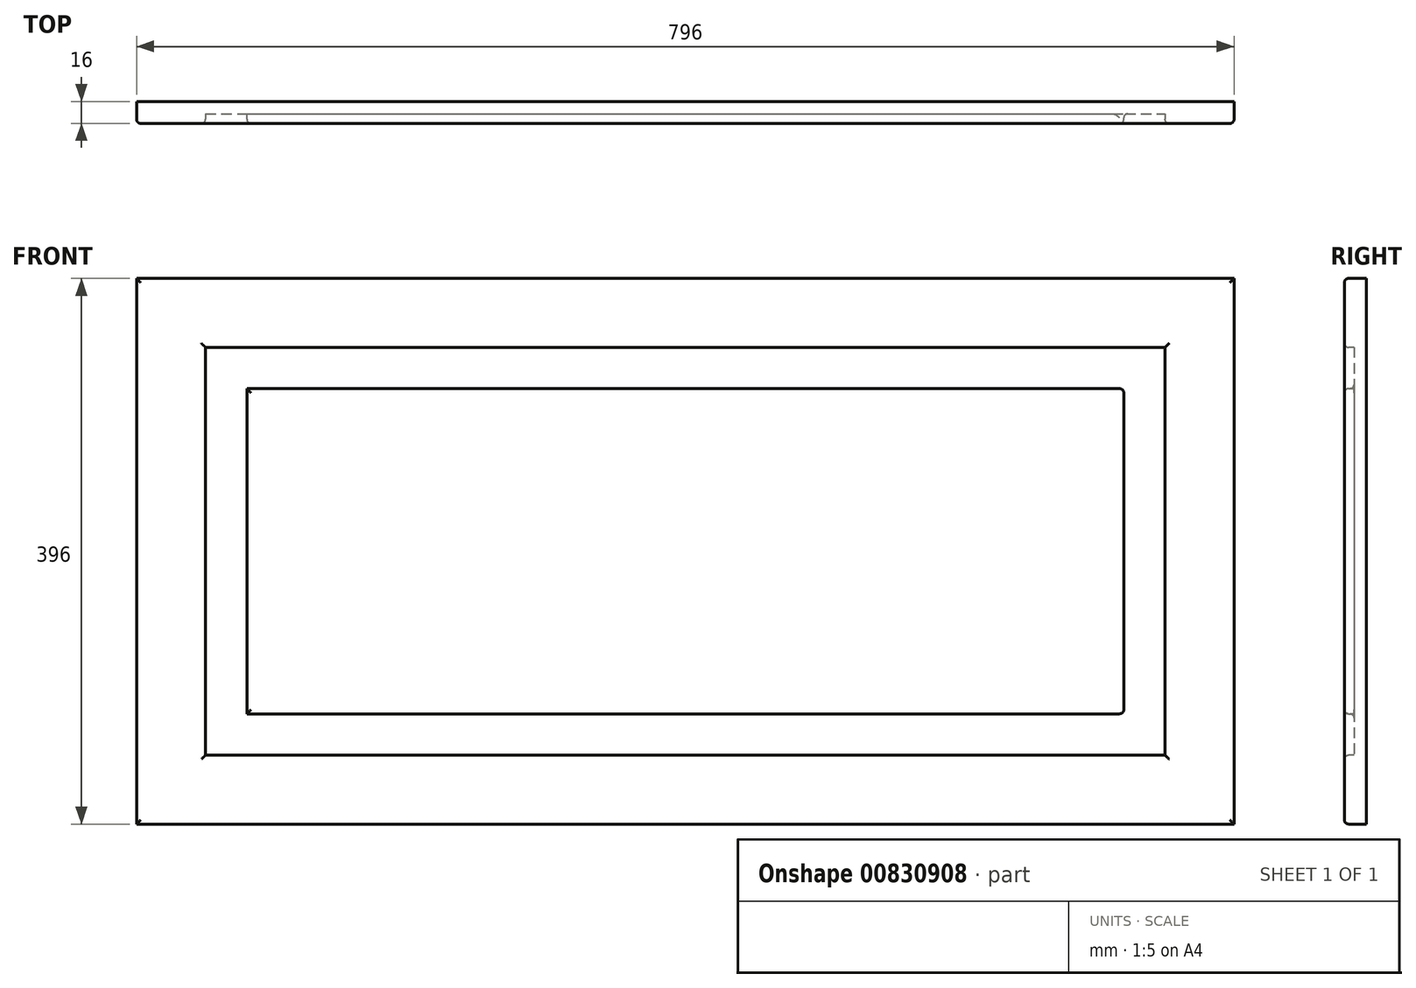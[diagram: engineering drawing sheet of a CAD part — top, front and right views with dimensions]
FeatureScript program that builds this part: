
annotation { "Feature Type Name" : "Feature", "Feature Type Description" : "" }
export const myFeature = defineFeature(function(context is Context, id is Id, definition is map)
    precondition{}
    {
        {
            var Q0;
            Q0=qCreatedBy(makeId("Front.planeOp"),FACE);
            var sketch = newSketch(context, id + "F0", { "sketchPlane" : qUnion([Q0])});
            skLineSegment(sketch, "E0.bottom", {"start": v(0, 0) * mm, "end": v(44.66, 0) * mm});
            skLineSegment(sketch, "E0.top", {"start": v(0, 33.8) * mm, "end": v(44.66, 33.8) * mm});
            skLineSegment(sketch, "E0.left", {"start": v(0, 0) * mm, "end": v(0, 33.8) * mm});
            skLineSegment(sketch, "E0.right", {"start": v(44.66, 0) * mm, "end": v(44.66, 33.8) * mm});
            skSolve(sketch);
        }
        {
            var Q0;
            Q0=makeQuery(id+"F0.imprint","IMPRINT",FACE,{"disambiguationData":[TD([[makeQuery(id+"F0.imprint","IMPRINT",EDGE,{"derivedFrom":sQuery(id+"F0.wireOp",EDGE,"E0.bottom")}),1.0]])]});
            extrude(context, id + "F1", {"entities" : qUnion([Q0]), "depth" : 16 * mm, "offsetDistance" : 25.4 * mm});
        }
        {
            var Q0;
            Q0=makeQuery(id+"F1.opExtrude","SWEPT_FACE",FACE,{"disambiguationData":[OSD([sQuery(id+"F0.wireOp",EDGE,"E0.bottom")])]});
            extrude(context, id + "F2", {"entities" : qUnion([Q0]), "operationType" : NewBodyOperationType.ADD, "oppositeDirection" : true, "depth" : 796 * mm, "offsetDistance" : 25 * mm});
        }
        {
            var Q0;
            {var subQ0=sQuery(id+"F0.wireOp",EDGE,"E0.left");Q0=makeQuery(id+"F2.boolean.opBoolean","MERGE",FACE,{"derivedFrom":[makeQuery(id+"F1.opExtrude","SWEPT_FACE",FACE,{"disambiguationData":[OSD([subQ0])]}),makeQuery(id+"F2.opExtrude","SWEPT_FACE",FACE,{"disambiguationData":[OSD([sQuery(id+"F0.wireOp",EDGE,"E0.bottom"),subQ0])]})]});}
            extrude(context, id + "F3", {"entities" : qUnion([Q0]), "operationType" : NewBodyOperationType.ADD, "oppositeDirection" : true, "depth" : 196 * mm, "offsetDistance" : 25 * mm});
        }
        {
            var Q0;
            {var subQ0=sQuery(id+"F0.wireOp",EDGE,"E0.left");var subQ1=sQuery(id+"F0.wireOp",EDGE,"E0.bottom");Q0=makeQuery(id+"F3.boolean.opBoolean","MERGE",FACE,{"derivedFrom":[makeQuery(id+"F2.boolean.opBoolean","MERGE",FACE,{"derivedFrom":[makeQuery(id+"F1.opExtrude","CAP_FACE",FACE,{"disambiguationData":[OSD([subQ1,sQuery(id+"F0.wireOp",EDGE,"E0.top"),subQ0,sQuery(id+"F0.wireOp",EDGE,"E0.right")])],"isStart":false}),makeQuery(id+"F2.opExtrude","SWEPT_FACE",FACE,{"disambiguationData":[OSD([subQ1]),TDD([makeQuery(id+"F1.opExtrude","CAP_EDGE",EDGE,{"disambiguationData":[OSD([subQ1])],"isStart":false})])]})]}),makeQuery(id+"F3.opExtrude","SWEPT_FACE",FACE,{"disambiguationData":[OSD([subQ1,subQ0]),TDD([makeQuery(id+"F2.boolean.opBoolean","MERGE",EDGE,{"derivedFrom":[makeQuery(id+"F1.opExtrude","CAP_EDGE",EDGE,{"disambiguationData":[OSD([subQ0])],"isStart":false}),makeQuery(id+"F2.opExtrude","SWEPT_EDGE",EDGE,{"disambiguationData":[OSD([subQ1,subQ0]),TDD([makeQuery(id+"F1.opExtrude","CAP_VERTEX",VERTEX,{"disambiguationData":[OSD([subQ1,subQ0])],"isStart":false})])]})]})])]})]});}
            var sketch = newSketch(context, id + "F4", { "sketchPlane" : qUnion([Q0])});
            skLineSegment(sketch, "E1.bottom", {"start": v(59.7, 646.67) * mm, "end": v(128.66, 646.67) * mm});
            skLineSegment(sketch, "E1.top", {"start": v(59.7, 152.97) * mm, "end": v(128.66, 152.97) * mm});
            skLineSegment(sketch, "E1.left", {"start": v(59.7, 646.67) * mm, "end": v(59.7, 152.97) * mm});
            skLineSegment(sketch, "E1.right", {"start": v(128.66, 646.67) * mm, "end": v(128.66, 152.97) * mm});
            skSolve(sketch);
        }
        {
            var Q0;
            Q0=makeQuery(id+"F4.imprint","IMPRINT",FACE,{"disambiguationData":[TD([[makeQuery(id+"F4.imprint","IMPRINT",EDGE,{"derivedFrom":sQuery(id+"F4.wireOp",EDGE,"E1.bottom")}),-1.0]])]});
            extrude(context, id + "F5", {"entities" : qUnion([Q0]), "operationType" : NewBodyOperationType.REMOVE, "oppositeDirection" : true, "depth" : 7 * mm, "offsetDistance" : 25 * mm});
        }
        {
            var Q0;
            Q0=makeQuery(id+"F5.boolean.opBoolean","COPY",FACE,{"derivedFrom":makeQuery(id+"F5.opExtrude","SWEPT_FACE",FACE,{"disambiguationData":[OSD([sQuery(id+"F4.wireOp",EDGE,"E1.left")])]})});
            extrude(context, id + "F6", {"entities" : qUnion([Q0]), "operationType" : NewBodyOperationType.REMOVE, "oppositeDirection" : true, "depth" : 9.7 * mm, "offsetDistance" : 25 * mm});
        }
        {
            var Q0;
            {var subQ0=sQuery(id+"F4.wireOp",EDGE,"E1.bottom");Q0=makeQuery(id+"F6.boolean.opBoolean","MERGE",FACE,{"derivedFrom":[makeQuery(id+"F5.boolean.opBoolean","COPY",FACE,{"derivedFrom":makeQuery(id+"F5.opExtrude","SWEPT_FACE",FACE,{"disambiguationData":[OSD([subQ0])]})}),makeQuery(id+"F6.opExtrude","SWEPT_FACE",FACE,{"disambiguationData":[OSD([subQ0,sQuery(id+"F4.wireOp",EDGE,"E1.left")])]})]});}
            extrude(context, id + "F7", {"entities" : qUnion([Q0]), "operationType" : NewBodyOperationType.ADD, "oppositeDirection" : true, "depth" : 99.33 * mm, "offsetDistance" : 25 * mm});
        }
        {
            var Q0;
            {var subQ0=sQuery(id+"F4.wireOp",EDGE,"E1.bottom");Q0=makeQuery(id+"F6.boolean.opBoolean","MERGE",FACE,{"derivedFrom":[makeQuery(id+"F5.boolean.opBoolean","COPY",FACE,{"derivedFrom":makeQuery(id+"F5.opExtrude","SWEPT_FACE",FACE,{"disambiguationData":[OSD([subQ0])]})}),makeQuery(id+"F6.opExtrude","SWEPT_FACE",FACE,{"disambiguationData":[OSD([subQ0,sQuery(id+"F4.wireOp",EDGE,"E1.left")])]})]});}
            extrude(context, id + "F8", {"entities" : qUnion([Q0]), "operationType" : NewBodyOperationType.REMOVE, "oppositeDirection" : true, "depth" : 99.33 * mm, "offsetDistance" : 25 * mm});
        }
        {
            var Q0;
            {var subQ0=sQuery(id+"F4.wireOp",EDGE,"E1.right");Q0=makeQuery(id+"F8.boolean.opBoolean","MERGE",FACE,{"derivedFrom":[makeQuery(id+"F5.boolean.opBoolean","COPY",FACE,{"derivedFrom":makeQuery(id+"F5.opExtrude","SWEPT_FACE",FACE,{"disambiguationData":[OSD([subQ0])]})}),makeQuery(id+"F8.opExtrude","SWEPT_FACE",FACE,{"disambiguationData":[OSD([sQuery(id+"F4.wireOp",EDGE,"E1.bottom"),subQ0])]})]});}
            extrude(context, id + "F9", {"entities" : qUnion([Q0]), "operationType" : NewBodyOperationType.REMOVE, "oppositeDirection" : true, "depth" : 17.34 * mm, "offsetDistance" : 25 * mm});
        }
        {
            var Q0;
            {var subQ0=sQuery(id+"F4.wireOp",EDGE,"E1.top");Q0=makeQuery(id+"F9.boolean.opBoolean","MERGE",FACE,{"derivedFrom":[makeQuery(id+"F6.boolean.opBoolean","MERGE",FACE,{"derivedFrom":[makeQuery(id+"F5.boolean.opBoolean","COPY",FACE,{"derivedFrom":makeQuery(id+"F5.opExtrude","SWEPT_FACE",FACE,{"disambiguationData":[OSD([subQ0])]})}),makeQuery(id+"F6.opExtrude","SWEPT_FACE",FACE,{"disambiguationData":[OSD([subQ0,sQuery(id+"F4.wireOp",EDGE,"E1.left")])]})]}),makeQuery(id+"F9.opExtrude","SWEPT_FACE",FACE,{"disambiguationData":[OSD([subQ0,sQuery(id+"F4.wireOp",EDGE,"E1.right")])]})]});}
            extrude(context, id + "F10", {"entities" : qUnion([Q0]), "operationType" : NewBodyOperationType.REMOVE, "oppositeDirection" : true, "depth" : 102.97 * mm, "offsetDistance" : 25 * mm});
        }
        {
            var Q0;
            {var subQ0=sQuery(id+"F4.wireOp",EDGE,"E1.right");var subQ1=sQuery(id+"F4.wireOp",EDGE,"E1.top");var subQ2=sQuery(id+"F4.wireOp",EDGE,"E1.left");var subQ3=sQuery(id+"F4.wireOp",EDGE,"E1.bottom");Q0=makeQuery(id+"F10.boolean.opBoolean","MERGE",FACE,{"derivedFrom":[makeQuery(id+"F9.boolean.opBoolean","MERGE",FACE,{"derivedFrom":[makeQuery(id+"F8.boolean.opBoolean","MERGE",FACE,{"derivedFrom":[makeQuery(id+"F6.boolean.opBoolean","MERGE",FACE,{"derivedFrom":[makeQuery(id+"F5.boolean.opBoolean","COPY",FACE,{"derivedFrom":makeQuery(id+"F5.opExtrude","CAP_FACE",FACE,{"disambiguationData":[OSD([subQ3,subQ1,subQ2,subQ0])],"isStart":false})}),makeQuery(id+"F6.opExtrude","SWEPT_FACE",FACE,{"disambiguationData":[OSD([subQ2]),TDD([makeQuery(id+"F5.boolean.opBoolean","COPY",EDGE,{"derivedFrom":makeQuery(id+"F5.opExtrude","CAP_EDGE",EDGE,{"disambiguationData":[OSD([subQ2])],"isStart":false})})])]})]}),makeQuery(id+"F8.opExtrude","SWEPT_FACE",FACE,{"disambiguationData":[OSD([subQ3,subQ2]),TDD([makeQuery(id+"F6.boolean.opBoolean","MERGE",EDGE,{"derivedFrom":[makeQuery(id+"F5.boolean.opBoolean","COPY",EDGE,{"derivedFrom":makeQuery(id+"F5.opExtrude","CAP_EDGE",EDGE,{"disambiguationData":[OSD([subQ3])],"isStart":false})}),makeQuery(id+"F6.opExtrude","SWEPT_EDGE",EDGE,{"disambiguationData":[OSD([subQ3,subQ2]),TDD([makeQuery(id+"F5.boolean.opBoolean","COPY",VERTEX,{"derivedFrom":makeQuery(id+"F5.opExtrude","CAP_VERTEX",VERTEX,{"disambiguationData":[OSD([subQ3,subQ2])],"isStart":false})})])]})]})])]})]}),makeQuery(id+"F9.opExtrude","SWEPT_FACE",FACE,{"disambiguationData":[OSD([subQ3,subQ0]),TDD([makeQuery(id+"F8.boolean.opBoolean","MERGE",EDGE,{"derivedFrom":[makeQuery(id+"F5.boolean.opBoolean","COPY",EDGE,{"derivedFrom":makeQuery(id+"F5.opExtrude","CAP_EDGE",EDGE,{"disambiguationData":[OSD([subQ0])],"isStart":false})}),makeQuery(id+"F8.opExtrude","SWEPT_EDGE",EDGE,{"disambiguationData":[OSD([subQ3,subQ0]),TDD([makeQuery(id+"F5.boolean.opBoolean","COPY",VERTEX,{"derivedFrom":makeQuery(id+"F5.opExtrude","CAP_VERTEX",VERTEX,{"disambiguationData":[OSD([subQ3,subQ0])],"isStart":false})})])]})]})])]})]}),makeQuery(id+"F10.opExtrude","SWEPT_FACE",FACE,{"disambiguationData":[OSD([subQ1,subQ2,subQ0]),TDD([makeQuery(id+"F9.boolean.opBoolean","MERGE",EDGE,{"derivedFrom":[makeQuery(id+"F6.boolean.opBoolean","MERGE",EDGE,{"derivedFrom":[makeQuery(id+"F5.boolean.opBoolean","COPY",EDGE,{"derivedFrom":makeQuery(id+"F5.opExtrude","CAP_EDGE",EDGE,{"disambiguationData":[OSD([subQ1])],"isStart":false})}),makeQuery(id+"F6.opExtrude","SWEPT_EDGE",EDGE,{"disambiguationData":[OSD([subQ1,subQ2]),TDD([makeQuery(id+"F5.boolean.opBoolean","COPY",VERTEX,{"derivedFrom":makeQuery(id+"F5.opExtrude","CAP_VERTEX",VERTEX,{"disambiguationData":[OSD([subQ1,subQ2])],"isStart":false})})])]})]}),makeQuery(id+"F9.opExtrude","SWEPT_EDGE",EDGE,{"disambiguationData":[OSD([subQ1,subQ0]),TDD([makeQuery(id+"F5.boolean.opBoolean","COPY",VERTEX,{"derivedFrom":makeQuery(id+"F5.opExtrude","CAP_VERTEX",VERTEX,{"disambiguationData":[OSD([subQ1,subQ0])],"isStart":false})})])]})]})])]})]});}
            var sketch = newSketch(context, id + "F11", { "sketchPlane" : qUnion([Q0])});
            skLineSegment(sketch, "E2.bottom", {"start": v(74.13, 678.73) * mm, "end": v(109.41, 678.73) * mm});
            skLineSegment(sketch, "E2.top", {"start": v(74.13, 186.63) * mm, "end": v(109.41, 186.63) * mm});
            skLineSegment(sketch, "E2.left", {"start": v(74.13, 678.73) * mm, "end": v(74.13, 186.63) * mm});
            skLineSegment(sketch, "E2.right", {"start": v(109.41, 678.73) * mm, "end": v(109.41, 186.63) * mm});
            skSolve(sketch);
        }
        {
            var Q0;
            Q0=makeQuery(id+"F11.imprint","IMPRINT",FACE,{"disambiguationData":[TD([[makeQuery(id+"F11.imprint","IMPRINT",EDGE,{"derivedFrom":sQuery(id+"F11.wireOp",EDGE,"E2.bottom")}),-1.0]])]});
            extrude(context, id + "F12", {"entities" : qUnion([Q0]), "operationType" : NewBodyOperationType.ADD, "depth" : 7 * mm, "offsetDistance" : 25 * mm});
        }
        {
            var Q0;
            Q0=makeQuery(id+"F12.opExtrude","SWEPT_FACE",FACE,{"disambiguationData":[OSD([sQuery(id+"F11.wireOp",EDGE,"E2.bottom")])]});
            extrude(context, id + "F13", {"entities" : qUnion([Q0]), "operationType" : NewBodyOperationType.ADD, "depth" : 37.27 * mm, "offsetDistance" : 25 * mm});
        }
        {
            var Q0;
            {var subQ0=sQuery(id+"F11.wireOp",EDGE,"E2.right");Q0=makeQuery(id+"F13.boolean.opBoolean","MERGE",FACE,{"derivedFrom":[makeQuery(id+"F12.opExtrude","SWEPT_FACE",FACE,{"disambiguationData":[OSD([subQ0])]}),makeQuery(id+"F13.opExtrude","SWEPT_FACE",FACE,{"disambiguationData":[OSD([sQuery(id+"F11.wireOp",EDGE,"E2.bottom"),subQ0])]})]});}
            extrude(context, id + "F14", {"entities" : qUnion([Q0]), "operationType" : NewBodyOperationType.ADD, "depth" : 6.58 * mm, "offsetDistance" : 25 * mm});
        }
        {
            var Q0;
            {var subQ0=sQuery(id+"F11.wireOp",EDGE,"E2.top");Q0=makeQuery(id+"F14.boolean.opBoolean","MERGE",FACE,{"derivedFrom":[makeQuery(id+"F12.opExtrude","SWEPT_FACE",FACE,{"disambiguationData":[OSD([subQ0])]}),makeQuery(id+"F14.opExtrude","SWEPT_FACE",FACE,{"disambiguationData":[OSD([subQ0,sQuery(id+"F11.wireOp",EDGE,"E2.right")])]})]});}
            extrude(context, id + "F15", {"entities" : qUnion([Q0]), "operationType" : NewBodyOperationType.ADD, "depth" : 106.63 * mm, "offsetDistance" : 25 * mm});
        }
        {
            var Q0;
            {var subQ0=sQuery(id+"F11.wireOp",EDGE,"E2.left");Q0=makeQuery(id+"F15.boolean.opBoolean","MERGE",FACE,{"derivedFrom":[makeQuery(id+"F13.boolean.opBoolean","MERGE",FACE,{"derivedFrom":[makeQuery(id+"F12.opExtrude","SWEPT_FACE",FACE,{"disambiguationData":[OSD([subQ0])]}),makeQuery(id+"F13.opExtrude","SWEPT_FACE",FACE,{"disambiguationData":[OSD([sQuery(id+"F11.wireOp",EDGE,"E2.bottom"),subQ0])]})]}),makeQuery(id+"F15.opExtrude","SWEPT_FACE",FACE,{"disambiguationData":[OSD([sQuery(id+"F11.wireOp",EDGE,"E2.top"),subQ0])]})]});}
            extrude(context, id + "F16", {"entities" : qUnion([Q0]), "operationType" : NewBodyOperationType.REMOVE, "oppositeDirection" : true, "depth" : 5.87 * mm, "offsetDistance" : 25 * mm});
        }
        {
            var Q0;
            Q0=makeQuery(id+"F3.opExtrude","CAP_FACE",FACE,{"disambiguationData":[OSD([sQuery(id+"F0.wireOp",EDGE,"E0.bottom"),sQuery(id+"F0.wireOp",EDGE,"E0.left")])],"isStart":false});
            extrude(context, id + "F17", {"entities" : qUnion([Q0]), "operationType" : NewBodyOperationType.ADD, "depth" : 200 * mm, "offsetDistance" : 25 * mm});
        }
        {
            var Q0;
            {var subQ0=sQuery(id+"F4.wireOp",EDGE,"E1.right");Q0=makeQuery(id+"F10.boolean.opBoolean","MERGE",FACE,{"derivedFrom":[makeQuery(id+"F9.boolean.opBoolean","COPY",FACE,{"derivedFrom":makeQuery(id+"F9.opExtrude","CAP_FACE",FACE,{"disambiguationData":[OSD([sQuery(id+"F4.wireOp",EDGE,"E1.bottom"),subQ0])],"isStart":false})}),makeQuery(id+"F10.opExtrude","SWEPT_FACE",FACE,{"disambiguationData":[OSD([sQuery(id+"F4.wireOp",EDGE,"E1.top"),subQ0])]})]});}
            extrude(context, id + "F18", {"entities" : qUnion([Q0]), "operationType" : NewBodyOperationType.REMOVE, "oppositeDirection" : true, "depth" : 200 * mm, "offsetDistance" : 25 * mm});
        }
        {
            var Q0;
            {var subQ0=sQuery(id+"F11.wireOp",EDGE,"E2.right");var subQ1=sQuery(id+"F11.wireOp",EDGE,"E2.top");Q0=makeQuery(id+"F15.boolean.opBoolean","MERGE",FACE,{"derivedFrom":[makeQuery(id+"F14.opExtrude","CAP_FACE",FACE,{"disambiguationData":[OSD([sQuery(id+"F11.wireOp",EDGE,"E2.bottom"),subQ0])],"isStart":false}),makeQuery(id+"F15.opExtrude","SWEPT_FACE",FACE,{"disambiguationData":[OSD([subQ1,subQ0]),TDD([makeQuery(id+"F14.opExtrude","CAP_EDGE",EDGE,{"disambiguationData":[OSD([subQ1,subQ0])],"isStart":false})])]})]});}
            extrude(context, id + "F19", {"entities" : qUnion([Q0]), "operationType" : NewBodyOperationType.ADD, "depth" : 200 * mm, "offsetDistance" : 25 * mm});
        }
        {
            var Q0;
            Q0=makeQuery(id+"F17.opExtrude","CAP_FACE",FACE,{"disambiguationData":[OSD([sQuery(id+"F0.wireOp",EDGE,"E0.bottom"),sQuery(id+"F0.wireOp",EDGE,"E0.left")])],"isStart":false});
            extrude(context, id + "F20", {"entities" : qUnion([Q0]), "operationType" : NewBodyOperationType.ADD, "depth" : 200 * mm, "offsetDistance" : 25 * mm});
        }
        {
            var Q0;
            Q0=makeQuery(id+"F18.boolean.opBoolean","COPY",FACE,{"derivedFrom":makeQuery(id+"F18.opExtrude","CAP_FACE",FACE,{"disambiguationData":[OSD([sQuery(id+"F4.wireOp",EDGE,"E1.bottom"),sQuery(id+"F4.wireOp",EDGE,"E1.top"),sQuery(id+"F4.wireOp",EDGE,"E1.right")])],"isStart":false})});
            extrude(context, id + "F21", {"entities" : qUnion([Q0]), "operationType" : NewBodyOperationType.REMOVE, "oppositeDirection" : true, "depth" : 200 * mm, "offsetDistance" : 25 * mm});
        }
        {
            var Q0;
            Q0=makeQuery(id+"F19.opExtrude","CAP_FACE",FACE,{"disambiguationData":[OSD([sQuery(id+"F11.wireOp",EDGE,"E2.bottom"),sQuery(id+"F11.wireOp",EDGE,"E2.top"),sQuery(id+"F11.wireOp",EDGE,"E2.right")])],"isStart":false});
            extrude(context, id + "F22", {"entities" : qUnion([Q0]), "operationType" : NewBodyOperationType.ADD, "depth" : 200 * mm, "offsetDistance" : 25 * mm});
        }
        {
            var Q0;
            {var subQ0=sQuery(id+"F11.wireOp",EDGE,"E2.right");var subQ1=sQuery(id+"F11.wireOp",EDGE,"E2.top");Q0=makeQuery(id+"F22.boolean.opBoolean","MERGE",FACE,{"derivedFrom":[makeQuery(id+"F19.boolean.opBoolean","MERGE",FACE,{"derivedFrom":[makeQuery(id+"F15.opExtrude","CAP_FACE",FACE,{"disambiguationData":[OSD([subQ1,subQ0])],"isStart":false}),makeQuery(id+"F19.opExtrude","SWEPT_FACE",FACE,{"disambiguationData":[OSD([subQ1,subQ0])]})]}),makeQuery(id+"F22.opExtrude","SWEPT_FACE",FACE,{"disambiguationData":[OSD([subQ1,subQ0])]})]});}
            extrude(context, id + "F23", {"entities" : qUnion([Q0]), "operationType" : NewBodyOperationType.REMOVE, "oppositeDirection" : true, "depth" : 600 * mm, "offsetDistance" : 25 * mm});
        }
        {
            var Q0;
            {var subQ0=sQuery(id+"F4.wireOp",EDGE,"E1.right");var subQ1=sQuery(id+"F4.wireOp",EDGE,"E1.top");Q0=makeQuery(id+"F21.boolean.opBoolean","MERGE",FACE,{"derivedFrom":[makeQuery(id+"F18.boolean.opBoolean","MERGE",FACE,{"derivedFrom":[makeQuery(id+"F10.boolean.opBoolean","COPY",FACE,{"derivedFrom":makeQuery(id+"F10.opExtrude","CAP_FACE",FACE,{"disambiguationData":[OSD([subQ1,sQuery(id+"F4.wireOp",EDGE,"E1.left"),subQ0])],"isStart":false})}),makeQuery(id+"F18.opExtrude","SWEPT_FACE",FACE,{"disambiguationData":[OSD([subQ1,subQ0])]})]}),makeQuery(id+"F21.opExtrude","SWEPT_FACE",FACE,{"disambiguationData":[OSD([subQ1,subQ0])]})]});}
            extrude(context, id + "F24", {"entities" : qUnion([Q0]), "operationType" : NewBodyOperationType.ADD, "depth" : 600 * mm, "offsetDistance" : 25 * mm});
        }
        {
            var Q0;
            {var subQ0=sQuery(id+"F0.wireOp",EDGE,"E0.left");var subQ1=sQuery(id+"F0.wireOp",EDGE,"E0.bottom");var subQ2=makeQuery(id+"F1.opExtrude","SWEPT_EDGE",EDGE,{"disambiguationData":[OSD([subQ1,subQ0])]});var subQ3=makeQuery(id+"F3.opExtrude","CAP_EDGE",EDGE,{"disambiguationData":[OSD([subQ1,subQ0]),TDD([subQ2])],"isStart":false});Q0=makeQuery(id+"F20.boolean.opBoolean","MERGE",FACE,{"derivedFrom":[makeQuery(id+"F17.boolean.opBoolean","MERGE",FACE,{"derivedFrom":[makeQuery(id+"F3.boolean.opBoolean","MERGE",FACE,{"derivedFrom":[makeQuery(id+"F1.opExtrude","SWEPT_FACE",FACE,{"disambiguationData":[OSD([subQ1])]}),makeQuery(id+"F3.opExtrude","SWEPT_FACE",FACE,{"disambiguationData":[OSD([subQ1,subQ0]),TDD([subQ2])]})]}),makeQuery(id+"F17.opExtrude","SWEPT_FACE",FACE,{"disambiguationData":[OSD([subQ1,subQ0]),TDD([subQ3])]})]}),makeQuery(id+"F20.opExtrude","SWEPT_FACE",FACE,{"disambiguationData":[OSD([subQ1,subQ0]),TDD([makeQuery(id+"F17.opExtrude","CAP_EDGE",EDGE,{"disambiguationData":[OSD([subQ1,subQ0]),TDD([subQ3])],"isStart":false})])]})]});}
            extrude(context, id + "F25", {"entities" : qUnion([Q0]), "operationType" : NewBodyOperationType.REMOVE, "oppositeDirection" : true, "depth" : 600 * mm, "offsetDistance" : 25 * mm});
        }
        {
            var Q0;
            Q0=makeQuery(id+"F25.boolean.opBoolean","COPY",FACE,{"derivedFrom":makeQuery(id+"F25.opExtrude","CAP_FACE",FACE,{"disambiguationData":[OSD([sQuery(id+"F0.wireOp",EDGE,"E0.bottom"),sQuery(id+"F0.wireOp",EDGE,"E0.left")])],"isStart":false})});
            extrude(context, id + "F26", {"entities" : qUnion([Q0]), "operationType" : NewBodyOperationType.ADD, "depth" : 200 * mm, "offsetDistance" : 25 * mm});
        }
        {
            var Q0;
            Q0=makeQuery(id+"F24.opExtrude","CAP_FACE",FACE,{"disambiguationData":[OSD([sQuery(id+"F4.wireOp",EDGE,"E1.top"),sQuery(id+"F4.wireOp",EDGE,"E1.left"),sQuery(id+"F4.wireOp",EDGE,"E1.right")])],"isStart":false});
            extrude(context, id + "F27", {"entities" : qUnion([Q0]), "operationType" : NewBodyOperationType.REMOVE, "oppositeDirection" : true, "depth" : 200 * mm, "offsetDistance" : 25 * mm});
        }
        {
            var Q0;
            Q0=makeQuery(id+"F23.boolean.opBoolean","COPY",FACE,{"derivedFrom":makeQuery(id+"F23.opExtrude","CAP_FACE",FACE,{"disambiguationData":[OSD([sQuery(id+"F11.wireOp",EDGE,"E2.top"),sQuery(id+"F11.wireOp",EDGE,"E2.right")])],"isStart":false})});
            extrude(context, id + "F28", {"entities" : qUnion([Q0]), "operationType" : NewBodyOperationType.ADD, "depth" : 200 * mm, "offsetDistance" : 25 * mm});
        }
        {
            var Q0;
            {var subQ0=sQuery(id+"F0.wireOp",EDGE,"E0.left");var subQ1=sQuery(id+"F0.wireOp",EDGE,"E0.bottom");Q0=makeQuery(id+"F26.boolean.opBoolean","MERGE",FACE,{"derivedFrom":[makeQuery(id+"F20.opExtrude","CAP_FACE",FACE,{"disambiguationData":[OSD([subQ1,subQ0])],"isStart":false}),makeQuery(id+"F26.opExtrude","SWEPT_FACE",FACE,{"disambiguationData":[OSD([subQ1,subQ0]),TDD([makeQuery(id+"F25.boolean.opBoolean","COPY",EDGE,{"derivedFrom":makeQuery(id+"F25.opExtrude","CAP_EDGE",EDGE,{"disambiguationData":[OSD([subQ1,subQ0]),TDD([makeQuery(id+"F20.opExtrude","CAP_EDGE",EDGE,{"disambiguationData":[OSD([subQ1,subQ0]),TDD([makeQuery(id+"F17.opExtrude","CAP_EDGE",EDGE,{"disambiguationData":[OSD([subQ1,subQ0]),TDD([makeQuery(id+"F3.opExtrude","CAP_EDGE",EDGE,{"disambiguationData":[OSD([subQ1,subQ0]),TDD([makeQuery(id+"F1.opExtrude","SWEPT_EDGE",EDGE,{"disambiguationData":[OSD([subQ1,subQ0])]})])],"isStart":false})])],"isStart":false})])],"isStart":false})])],"isStart":false})})])]})]});}
            extrude(context, id + "F29", {"entities" : qUnion([Q0]), "operationType" : NewBodyOperationType.ADD, "depth" : 200 * mm, "offsetDistance" : 25 * mm});
        }
        {
            var Q0;
            {var subQ0=sQuery(id+"F4.wireOp",EDGE,"E1.right");var subQ1=sQuery(id+"F4.wireOp",EDGE,"E1.top");Q0=makeQuery(id+"F27.boolean.opBoolean","MERGE",FACE,{"derivedFrom":[makeQuery(id+"F21.boolean.opBoolean","COPY",FACE,{"derivedFrom":makeQuery(id+"F21.opExtrude","CAP_FACE",FACE,{"disambiguationData":[OSD([sQuery(id+"F4.wireOp",EDGE,"E1.bottom"),subQ1,subQ0])],"isStart":false})}),makeQuery(id+"F27.opExtrude","SWEPT_FACE",FACE,{"disambiguationData":[OSD([subQ1,subQ0])]})]});}
            extrude(context, id + "F30", {"entities" : qUnion([Q0]), "operationType" : NewBodyOperationType.REMOVE, "oppositeDirection" : true, "depth" : 200 * mm, "offsetDistance" : 25 * mm});
        }
        {
            var Q0;
            {var subQ0=sQuery(id+"F11.wireOp",EDGE,"E2.right");var subQ1=sQuery(id+"F11.wireOp",EDGE,"E2.top");Q0=makeQuery(id+"F28.boolean.opBoolean","MERGE",FACE,{"derivedFrom":[makeQuery(id+"F22.opExtrude","CAP_FACE",FACE,{"disambiguationData":[OSD([sQuery(id+"F11.wireOp",EDGE,"E2.bottom"),subQ1,subQ0])],"isStart":false}),makeQuery(id+"F28.opExtrude","SWEPT_FACE",FACE,{"disambiguationData":[OSD([subQ1,subQ0]),TDD([makeQuery(id+"F23.boolean.opBoolean","COPY",EDGE,{"derivedFrom":makeQuery(id+"F23.opExtrude","CAP_EDGE",EDGE,{"disambiguationData":[OSD([subQ1,subQ0]),TDD([makeQuery(id+"F22.opExtrude","CAP_EDGE",EDGE,{"disambiguationData":[OSD([subQ1,subQ0])],"isStart":false})])],"isStart":false})})])]})]});}
            extrude(context, id + "F31", {"entities" : qUnion([Q0]), "operationType" : NewBodyOperationType.ADD, "depth" : 200 * mm, "offsetDistance" : 25 * mm});
        }
        {
            var Q0;
            {var subQ0=sQuery(id+"F11.wireOp",EDGE,"E2.right");var subQ1=sQuery(id+"F11.wireOp",EDGE,"E2.top");Q0=makeQuery(id+"F31.boolean.opBoolean","MERGE",FACE,{"derivedFrom":[makeQuery(id+"F28.opExtrude","CAP_FACE",FACE,{"disambiguationData":[OSD([subQ1,subQ0])],"isStart":false}),makeQuery(id+"F31.opExtrude","SWEPT_FACE",FACE,{"disambiguationData":[OSD([subQ1,subQ0])]})]});}
            extrude(context, id + "F32", {"entities" : qUnion([Q0]), "operationType" : NewBodyOperationType.REMOVE, "oppositeDirection" : true, "depth" : 200 * mm, "offsetDistance" : 25 * mm});
        }
        {
            var Q0;
            {var subQ0=sQuery(id+"F4.wireOp",EDGE,"E1.right");var subQ1=sQuery(id+"F4.wireOp",EDGE,"E1.top");Q0=makeQuery(id+"F30.boolean.opBoolean","MERGE",FACE,{"derivedFrom":[makeQuery(id+"F27.boolean.opBoolean","COPY",FACE,{"derivedFrom":makeQuery(id+"F27.opExtrude","CAP_FACE",FACE,{"disambiguationData":[OSD([subQ1,sQuery(id+"F4.wireOp",EDGE,"E1.left"),subQ0])],"isStart":false})}),makeQuery(id+"F30.opExtrude","SWEPT_FACE",FACE,{"disambiguationData":[OSD([subQ1,subQ0])]})]});}
            extrude(context, id + "F33", {"entities" : qUnion([Q0]), "operationType" : NewBodyOperationType.ADD, "depth" : 200 * mm, "offsetDistance" : 25 * mm});
        }
        {
            var Q0;
            {var subQ0=sQuery(id+"F0.wireOp",EDGE,"E0.left");var subQ1=sQuery(id+"F0.wireOp",EDGE,"E0.bottom");Q0=makeQuery(id+"F29.boolean.opBoolean","MERGE",FACE,{"derivedFrom":[makeQuery(id+"F26.opExtrude","CAP_FACE",FACE,{"disambiguationData":[OSD([subQ1,subQ0])],"isStart":false}),makeQuery(id+"F29.opExtrude","SWEPT_FACE",FACE,{"disambiguationData":[OSD([subQ1,subQ0]),TDD([makeQuery(id+"F26.opExtrude","CAP_EDGE",EDGE,{"disambiguationData":[OSD([subQ1,subQ0]),TDD([makeQuery(id+"F25.boolean.opBoolean","COPY",EDGE,{"derivedFrom":makeQuery(id+"F25.opExtrude","CAP_EDGE",EDGE,{"disambiguationData":[OSD([subQ1,subQ0]),TDD([makeQuery(id+"F20.opExtrude","CAP_EDGE",EDGE,{"disambiguationData":[OSD([subQ1,subQ0]),TDD([makeQuery(id+"F17.opExtrude","CAP_EDGE",EDGE,{"disambiguationData":[OSD([subQ1,subQ0]),TDD([makeQuery(id+"F3.opExtrude","CAP_EDGE",EDGE,{"disambiguationData":[OSD([subQ1,subQ0]),TDD([makeQuery(id+"F1.opExtrude","SWEPT_EDGE",EDGE,{"disambiguationData":[OSD([subQ1,subQ0])]})])],"isStart":false})])],"isStart":false})])],"isStart":false})])],"isStart":false})})])],"isStart":false})])]})]});}
            extrude(context, id + "F34", {"entities" : qUnion([Q0]), "operationType" : NewBodyOperationType.REMOVE, "oppositeDirection" : true, "depth" : 200 * mm, "offsetDistance" : 25 * mm});
        }
        {
            var Q0;
            Q0=makeQuery(id+"F34.boolean.opBoolean","COPY",FACE,{"derivedFrom":makeQuery(id+"F34.opExtrude","CAP_FACE",FACE,{"disambiguationData":[OSD([sQuery(id+"F0.wireOp",EDGE,"E0.bottom"),sQuery(id+"F0.wireOp",EDGE,"E0.left")])],"isStart":false})});
            extrude(context, id + "F35", {"entities" : qUnion([Q0]), "operationType" : NewBodyOperationType.ADD, "depth" : 200 * mm, "offsetDistance" : 25 * mm});
        }
        {
            var Q0;
            Q0=makeQuery(id+"F33.opExtrude","CAP_FACE",FACE,{"disambiguationData":[OSD([sQuery(id+"F4.wireOp",EDGE,"E1.top"),sQuery(id+"F4.wireOp",EDGE,"E1.left"),sQuery(id+"F4.wireOp",EDGE,"E1.right")])],"isStart":false});
            extrude(context, id + "F36", {"entities" : qUnion([Q0]), "operationType" : NewBodyOperationType.REMOVE, "oppositeDirection" : true, "depth" : 200 * mm, "offsetDistance" : 25 * mm});
        }
        {
            var Q0;
            Q0=makeQuery(id+"F32.boolean.opBoolean","COPY",FACE,{"derivedFrom":makeQuery(id+"F32.opExtrude","CAP_FACE",FACE,{"disambiguationData":[OSD([sQuery(id+"F11.wireOp",EDGE,"E2.top"),sQuery(id+"F11.wireOp",EDGE,"E2.right")])],"isStart":false})});
            extrude(context, id + "F37", {"entities" : qUnion([Q0]), "operationType" : NewBodyOperationType.ADD, "depth" : 200 * mm, "offsetDistance" : 25 * mm});
        }
        {
            var Q0;
            {var subQ0=sQuery(id+"F11.wireOp",EDGE,"E2.right");var subQ1=sQuery(id+"F11.wireOp",EDGE,"E2.top");var subQ2=makeQuery(id+"F12.opExtrude","CAP_VERTEX",VERTEX,{"disambiguationData":[OSD([subQ1,subQ0])],"isStart":false});var subQ3=makeQuery(id+"F14.opExtrude","CAP_VERTEX",VERTEX,{"disambiguationData":[OSD([subQ1,subQ0]),TDD([subQ2])],"isStart":false});var subQ4=makeQuery(id+"F15.opExtrude","CAP_VERTEX",VERTEX,{"disambiguationData":[OSD([subQ1,subQ0]),TDD([subQ3])],"isStart":false});var subQ5=makeQuery(id+"F19.opExtrude","CAP_VERTEX",VERTEX,{"disambiguationData":[OSD([subQ1,subQ0]),TDD([subQ4])],"isStart":false});var subQ6=makeQuery(id+"F23.boolean.opBoolean","COPY",VERTEX,{"derivedFrom":makeQuery(id+"F23.opExtrude","CAP_VERTEX",VERTEX,{"disambiguationData":[OSD([subQ1,subQ0]),TDD([makeQuery(id+"F22.opExtrude","CAP_VERTEX",VERTEX,{"disambiguationData":[OSD([subQ1,subQ0]),TDD([subQ5])],"isStart":false})])],"isStart":false})});var subQ7=makeQuery(id+"F14.boolean.opBoolean","MERGE",EDGE,{"derivedFrom":[makeQuery(id+"F12.opExtrude","CAP_EDGE",EDGE,{"disambiguationData":[OSD([subQ1])],"isStart":false}),makeQuery(id+"F14.opExtrude","SWEPT_EDGE",EDGE,{"disambiguationData":[OSD([subQ1,subQ0]),TDD([subQ2])]})]});var subQ8=makeQuery(id+"F23.boolean.opBoolean","COPY",EDGE,{"derivedFrom":makeQuery(id+"F23.opExtrude","CAP_EDGE",EDGE,{"disambiguationData":[OSD([subQ1,subQ0]),TDD([makeQuery(id+"F22.boolean.opBoolean","MERGE",EDGE,{"derivedFrom":[makeQuery(id+"F19.boolean.opBoolean","MERGE",EDGE,{"derivedFrom":[makeQuery(id+"F15.opExtrude","CAP_EDGE",EDGE,{"disambiguationData":[OSD([subQ1,subQ0]),TDD([subQ7])],"isStart":false}),makeQuery(id+"F19.opExtrude","SWEPT_EDGE",EDGE,{"disambiguationData":[OSD([subQ1,subQ0]),TDD([subQ4])]})]}),makeQuery(id+"F22.opExtrude","SWEPT_EDGE",EDGE,{"disambiguationData":[OSD([subQ1,subQ0]),TDD([subQ5])]})]})])],"isStart":false})});var subQ9=sQuery(id+"F11.wireOp",EDGE,"E2.bottom");var subQ10=makeQuery(id+"F13.boolean.opBoolean","MERGE",EDGE,{"derivedFrom":[makeQuery(id+"F12.opExtrude","CAP_EDGE",EDGE,{"disambiguationData":[OSD([subQ0])],"isStart":false}),makeQuery(id+"F13.opExtrude","SWEPT_EDGE",EDGE,{"disambiguationData":[OSD([subQ9,subQ0]),TDD([makeQuery(id+"F12.opExtrude","CAP_VERTEX",VERTEX,{"disambiguationData":[OSD([subQ9,subQ0])],"isStart":false})])]})]});var subQ11=makeQuery(id+"F15.boolean.opBoolean","MERGE",EDGE,{"derivedFrom":[makeQuery(id+"F14.opExtrude","CAP_EDGE",EDGE,{"disambiguationData":[OSD([subQ9,subQ0]),TDD([subQ10])],"isStart":false}),makeQuery(id+"F15.opExtrude","SWEPT_EDGE",EDGE,{"disambiguationData":[OSD([subQ1,subQ0]),TDD([subQ3])]})]});var subQ12=makeQuery(id+"F19.opExtrude","CAP_EDGE",EDGE,{"disambiguationData":[OSD([subQ9,subQ1,subQ0]),TDD([subQ11])],"isStart":false});Q0=makeQuery(id+"F37.boolean.opBoolean","MERGE",FACE,{"derivedFrom":[makeQuery(id+"F31.boolean.opBoolean","MERGE",FACE,{"derivedFrom":[makeQuery(id+"F28.boolean.opBoolean","MERGE",FACE,{"derivedFrom":[makeQuery(id+"F22.boolean.opBoolean","MERGE",FACE,{"derivedFrom":[makeQuery(id+"F19.boolean.opBoolean","MERGE",FACE,{"derivedFrom":[makeQuery(id+"F15.boolean.opBoolean","MERGE",FACE,{"derivedFrom":[makeQuery(id+"F14.boolean.opBoolean","MERGE",FACE,{"derivedFrom":[makeQuery(id+"F13.boolean.opBoolean","MERGE",FACE,{"derivedFrom":[makeQuery(id+"F12.opExtrude","CAP_FACE",FACE,{"disambiguationData":[OSD([subQ9,subQ1,sQuery(id+"F11.wireOp",EDGE,"E2.left"),subQ0])],"isStart":false}),makeQuery(id+"F13.opExtrude","SWEPT_FACE",FACE,{"disambiguationData":[OSD([subQ9]),TDD([makeQuery(id+"F12.opExtrude","CAP_EDGE",EDGE,{"disambiguationData":[OSD([subQ9])],"isStart":false})])]})]}),makeQuery(id+"F14.opExtrude","SWEPT_FACE",FACE,{"disambiguationData":[OSD([subQ9,subQ0]),TDD([subQ10])]})]}),makeQuery(id+"F15.opExtrude","SWEPT_FACE",FACE,{"disambiguationData":[OSD([subQ1,subQ0]),TDD([subQ7])]})]}),makeQuery(id+"F19.opExtrude","SWEPT_FACE",FACE,{"disambiguationData":[OSD([subQ9,subQ1,subQ0]),TDD([subQ11])]})]}),makeQuery(id+"F22.opExtrude","SWEPT_FACE",FACE,{"disambiguationData":[OSD([subQ9,subQ1,subQ0]),TDD([subQ12])]})]}),makeQuery(id+"F28.opExtrude","SWEPT_FACE",FACE,{"disambiguationData":[OSD([subQ1,subQ0]),TDD([subQ8])]})]}),makeQuery(id+"F31.opExtrude","SWEPT_FACE",FACE,{"disambiguationData":[OSD([subQ9,subQ1,subQ0]),TDD([makeQuery(id+"F28.boolean.opBoolean","MERGE",EDGE,{"derivedFrom":[makeQuery(id+"F22.opExtrude","CAP_EDGE",EDGE,{"disambiguationData":[OSD([subQ9,subQ1,subQ0]),TDD([subQ12])],"isStart":false}),makeQuery(id+"F28.opExtrude","SWEPT_EDGE",EDGE,{"disambiguationData":[OSD([subQ1,subQ0]),TDD([subQ6])]})]})])]})]}),makeQuery(id+"F37.opExtrude","SWEPT_FACE",FACE,{"disambiguationData":[OSD([subQ1,subQ0]),TDD([makeQuery(id+"F32.boolean.opBoolean","COPY",EDGE,{"derivedFrom":makeQuery(id+"F32.opExtrude","CAP_EDGE",EDGE,{"disambiguationData":[OSD([subQ1,subQ0]),TDD([makeQuery(id+"F31.boolean.opBoolean","MERGE",EDGE,{"derivedFrom":[makeQuery(id+"F28.opExtrude","CAP_EDGE",EDGE,{"disambiguationData":[OSD([subQ1,subQ0]),TDD([subQ8])],"isStart":false}),makeQuery(id+"F31.opExtrude","SWEPT_EDGE",EDGE,{"disambiguationData":[OSD([subQ1,subQ0]),TDD([makeQuery(id+"F28.opExtrude","CAP_VERTEX",VERTEX,{"disambiguationData":[OSD([subQ1,subQ0]),TDD([subQ6])],"isStart":false})])]})]})])],"isStart":false})})])]})]});}
            var Q1;
            {var subQ0=sQuery(id+"F0.wireOp",EDGE,"E0.left");var subQ1=sQuery(id+"F0.wireOp",EDGE,"E0.bottom");var subQ2=makeQuery(id+"F1.opExtrude","CAP_VERTEX",VERTEX,{"disambiguationData":[OSD([subQ1,subQ0])],"isStart":false});var subQ3=makeQuery(id+"F3.opExtrude","CAP_VERTEX",VERTEX,{"disambiguationData":[OSD([subQ1,subQ0]),TDD([subQ2])],"isStart":false});var subQ4=makeQuery(id+"F17.opExtrude","CAP_VERTEX",VERTEX,{"disambiguationData":[OSD([subQ1,subQ0]),TDD([subQ3])],"isStart":false});var subQ5=makeQuery(id+"F25.boolean.opBoolean","COPY",VERTEX,{"derivedFrom":makeQuery(id+"F25.opExtrude","CAP_VERTEX",VERTEX,{"disambiguationData":[OSD([subQ1,subQ0]),TDD([makeQuery(id+"F20.opExtrude","CAP_VERTEX",VERTEX,{"disambiguationData":[OSD([subQ1,subQ0]),TDD([subQ4])],"isStart":false})])],"isStart":false})});var subQ6=makeQuery(id+"F1.opExtrude","CAP_EDGE",EDGE,{"disambiguationData":[OSD([subQ1])],"isStart":false});var subQ7=makeQuery(id+"F25.boolean.opBoolean","COPY",EDGE,{"derivedFrom":makeQuery(id+"F25.opExtrude","CAP_EDGE",EDGE,{"disambiguationData":[OSD([subQ1,subQ0]),TDD([makeQuery(id+"F20.boolean.opBoolean","MERGE",EDGE,{"derivedFrom":[makeQuery(id+"F17.boolean.opBoolean","MERGE",EDGE,{"derivedFrom":[makeQuery(id+"F3.boolean.opBoolean","MERGE",EDGE,{"derivedFrom":[subQ6,makeQuery(id+"F3.opExtrude","SWEPT_EDGE",EDGE,{"disambiguationData":[OSD([subQ1,subQ0]),TDD([subQ2])]})]}),makeQuery(id+"F17.opExtrude","SWEPT_EDGE",EDGE,{"disambiguationData":[OSD([subQ1,subQ0]),TDD([subQ3])]})]}),makeQuery(id+"F20.opExtrude","SWEPT_EDGE",EDGE,{"disambiguationData":[OSD([subQ1,subQ0]),TDD([subQ4])]})]})])],"isStart":false})});var subQ8=sQuery(id+"F4.wireOp",EDGE,"E1.right");var subQ9=sQuery(id+"F4.wireOp",EDGE,"E1.top");var subQ10=makeQuery(id+"F5.boolean.opBoolean","COPY",VERTEX,{"derivedFrom":makeQuery(id+"F5.opExtrude","CAP_VERTEX",VERTEX,{"disambiguationData":[OSD([subQ9,subQ8])],"isStart":true})});var subQ11=makeQuery(id+"F10.boolean.opBoolean","COPY",VERTEX,{"derivedFrom":makeQuery(id+"F10.opExtrude","CAP_VERTEX",VERTEX,{"disambiguationData":[OSD([subQ9,subQ8]),TDD([makeQuery(id+"F9.boolean.opBoolean","COPY",VERTEX,{"derivedFrom":makeQuery(id+"F9.opExtrude","CAP_VERTEX",VERTEX,{"disambiguationData":[OSD([subQ9,subQ8]),TDD([subQ10])],"isStart":false})})])],"isStart":false})});var subQ12=makeQuery(id+"F18.boolean.opBoolean","COPY",VERTEX,{"derivedFrom":makeQuery(id+"F18.opExtrude","CAP_VERTEX",VERTEX,{"disambiguationData":[OSD([subQ9,subQ8]),TDD([subQ11])],"isStart":false})});var subQ13=sQuery(id+"F4.wireOp",EDGE,"E1.left");var subQ14=makeQuery(id+"F21.boolean.opBoolean","MERGE",EDGE,{"derivedFrom":[makeQuery(id+"F18.boolean.opBoolean","MERGE",EDGE,{"derivedFrom":[makeQuery(id+"F10.boolean.opBoolean","COPY",EDGE,{"derivedFrom":makeQuery(id+"F10.opExtrude","CAP_EDGE",EDGE,{"disambiguationData":[OSD([subQ9,subQ13,subQ8]),TDD([makeQuery(id+"F9.boolean.opBoolean","MERGE",EDGE,{"derivedFrom":[makeQuery(id+"F6.boolean.opBoolean","MERGE",EDGE,{"derivedFrom":[makeQuery(id+"F5.boolean.opBoolean","COPY",EDGE,{"derivedFrom":makeQuery(id+"F5.opExtrude","CAP_EDGE",EDGE,{"disambiguationData":[OSD([subQ9])],"isStart":true})}),makeQuery(id+"F6.opExtrude","SWEPT_EDGE",EDGE,{"disambiguationData":[OSD([subQ9,subQ13]),TDD([makeQuery(id+"F5.boolean.opBoolean","COPY",VERTEX,{"derivedFrom":makeQuery(id+"F5.opExtrude","CAP_VERTEX",VERTEX,{"disambiguationData":[OSD([subQ9,subQ13])],"isStart":true})})])]})]}),makeQuery(id+"F9.opExtrude","SWEPT_EDGE",EDGE,{"disambiguationData":[OSD([subQ9,subQ8]),TDD([subQ10])]})]})])],"isStart":false})}),makeQuery(id+"F18.opExtrude","SWEPT_EDGE",EDGE,{"disambiguationData":[OSD([subQ9,subQ8]),TDD([subQ11])]})]}),makeQuery(id+"F21.opExtrude","SWEPT_EDGE",EDGE,{"disambiguationData":[OSD([subQ9,subQ8]),TDD([subQ12])]})]});var subQ15=makeQuery(id+"F2.boolean.opBoolean","MERGE",EDGE,{"derivedFrom":[makeQuery(id+"F1.opExtrude","CAP_EDGE",EDGE,{"disambiguationData":[OSD([subQ0])],"isStart":false}),makeQuery(id+"F2.opExtrude","SWEPT_EDGE",EDGE,{"disambiguationData":[OSD([subQ1,subQ0]),TDD([subQ2])]})]});var subQ16=makeQuery(id+"F3.opExtrude","CAP_EDGE",EDGE,{"disambiguationData":[OSD([subQ1,subQ0]),TDD([subQ15])],"isStart":false});var subQ17=makeQuery(id+"F17.opExtrude","CAP_EDGE",EDGE,{"disambiguationData":[OSD([subQ1,subQ0]),TDD([subQ16])],"isStart":false});Q1=makeQuery(id+"F35.boolean.opBoolean","MERGE",FACE,{"derivedFrom":[makeQuery(id+"F33.boolean.opBoolean","MERGE",FACE,{"derivedFrom":[makeQuery(id+"F29.boolean.opBoolean","MERGE",FACE,{"derivedFrom":[makeQuery(id+"F26.boolean.opBoolean","MERGE",FACE,{"derivedFrom":[makeQuery(id+"F24.boolean.opBoolean","MERGE",FACE,{"derivedFrom":[makeQuery(id+"F20.boolean.opBoolean","MERGE",FACE,{"derivedFrom":[makeQuery(id+"F17.boolean.opBoolean","MERGE",FACE,{"derivedFrom":[makeQuery(id+"F3.boolean.opBoolean","MERGE",FACE,{"derivedFrom":[makeQuery(id+"F2.boolean.opBoolean","MERGE",FACE,{"derivedFrom":[makeQuery(id+"F1.opExtrude","CAP_FACE",FACE,{"disambiguationData":[OSD([subQ1,sQuery(id+"F0.wireOp",EDGE,"E0.top"),subQ0,sQuery(id+"F0.wireOp",EDGE,"E0.right")])],"isStart":false}),makeQuery(id+"F2.opExtrude","SWEPT_FACE",FACE,{"disambiguationData":[OSD([subQ1]),TDD([subQ6])]})]}),makeQuery(id+"F3.opExtrude","SWEPT_FACE",FACE,{"disambiguationData":[OSD([subQ1,subQ0]),TDD([subQ15])]})]}),makeQuery(id+"F17.opExtrude","SWEPT_FACE",FACE,{"disambiguationData":[OSD([subQ1,subQ0]),TDD([subQ16])]})]}),makeQuery(id+"F20.opExtrude","SWEPT_FACE",FACE,{"disambiguationData":[OSD([subQ1,subQ0]),TDD([subQ17])]})]}),makeQuery(id+"F24.opExtrude","SWEPT_FACE",FACE,{"disambiguationData":[OSD([subQ9,subQ13,subQ8]),TDD([subQ14])]})]}),makeQuery(id+"F26.opExtrude","SWEPT_FACE",FACE,{"disambiguationData":[OSD([subQ1,subQ0]),TDD([subQ7])]})]}),makeQuery(id+"F29.opExtrude","SWEPT_FACE",FACE,{"disambiguationData":[OSD([subQ1,subQ0]),TDD([makeQuery(id+"F26.boolean.opBoolean","MERGE",EDGE,{"derivedFrom":[makeQuery(id+"F20.opExtrude","CAP_EDGE",EDGE,{"disambiguationData":[OSD([subQ1,subQ0]),TDD([subQ17])],"isStart":false}),makeQuery(id+"F26.opExtrude","SWEPT_EDGE",EDGE,{"disambiguationData":[OSD([subQ1,subQ0]),TDD([subQ5])]})]})])]})]}),makeQuery(id+"F33.opExtrude","SWEPT_FACE",FACE,{"disambiguationData":[OSD([subQ9,subQ13,subQ8]),TDD([makeQuery(id+"F30.boolean.opBoolean","MERGE",EDGE,{"derivedFrom":[makeQuery(id+"F27.boolean.opBoolean","COPY",EDGE,{"derivedFrom":makeQuery(id+"F27.opExtrude","CAP_EDGE",EDGE,{"disambiguationData":[OSD([subQ9,subQ13,subQ8]),TDD([makeQuery(id+"F24.opExtrude","CAP_EDGE",EDGE,{"disambiguationData":[OSD([subQ9,subQ13,subQ8]),TDD([subQ14])],"isStart":false})])],"isStart":false})}),makeQuery(id+"F30.opExtrude","SWEPT_EDGE",EDGE,{"disambiguationData":[OSD([subQ9,subQ8]),TDD([makeQuery(id+"F27.boolean.opBoolean","COPY",VERTEX,{"derivedFrom":makeQuery(id+"F27.opExtrude","CAP_VERTEX",VERTEX,{"disambiguationData":[OSD([subQ9,subQ8]),TDD([makeQuery(id+"F24.opExtrude","CAP_VERTEX",VERTEX,{"disambiguationData":[OSD([subQ9,subQ8]),TDD([makeQuery(id+"F21.boolean.opBoolean","COPY",VERTEX,{"derivedFrom":makeQuery(id+"F21.opExtrude","CAP_VERTEX",VERTEX,{"disambiguationData":[OSD([subQ9,subQ8]),TDD([subQ12])],"isStart":false})})])],"isStart":false})])],"isStart":false})})])]})]})])]})]}),makeQuery(id+"F35.opExtrude","SWEPT_FACE",FACE,{"disambiguationData":[OSD([subQ1,subQ0]),TDD([makeQuery(id+"F34.boolean.opBoolean","COPY",EDGE,{"derivedFrom":makeQuery(id+"F34.opExtrude","CAP_EDGE",EDGE,{"disambiguationData":[OSD([subQ1,subQ0]),TDD([makeQuery(id+"F29.boolean.opBoolean","MERGE",EDGE,{"derivedFrom":[makeQuery(id+"F26.opExtrude","CAP_EDGE",EDGE,{"disambiguationData":[OSD([subQ1,subQ0]),TDD([subQ7])],"isStart":false}),makeQuery(id+"F29.opExtrude","SWEPT_EDGE",EDGE,{"disambiguationData":[OSD([subQ1,subQ0]),TDD([makeQuery(id+"F26.opExtrude","CAP_VERTEX",VERTEX,{"disambiguationData":[OSD([subQ1,subQ0]),TDD([subQ5])],"isStart":false})])]})]})])],"isStart":false})})])]})]});}
            fillet(context, id + "F38", {"entities" : qUnion([Q0, Q1]), "radius" : 3 * mm, "tangentPropagation" : true, "allowEdgeOverflow" : false});
        }
    });
